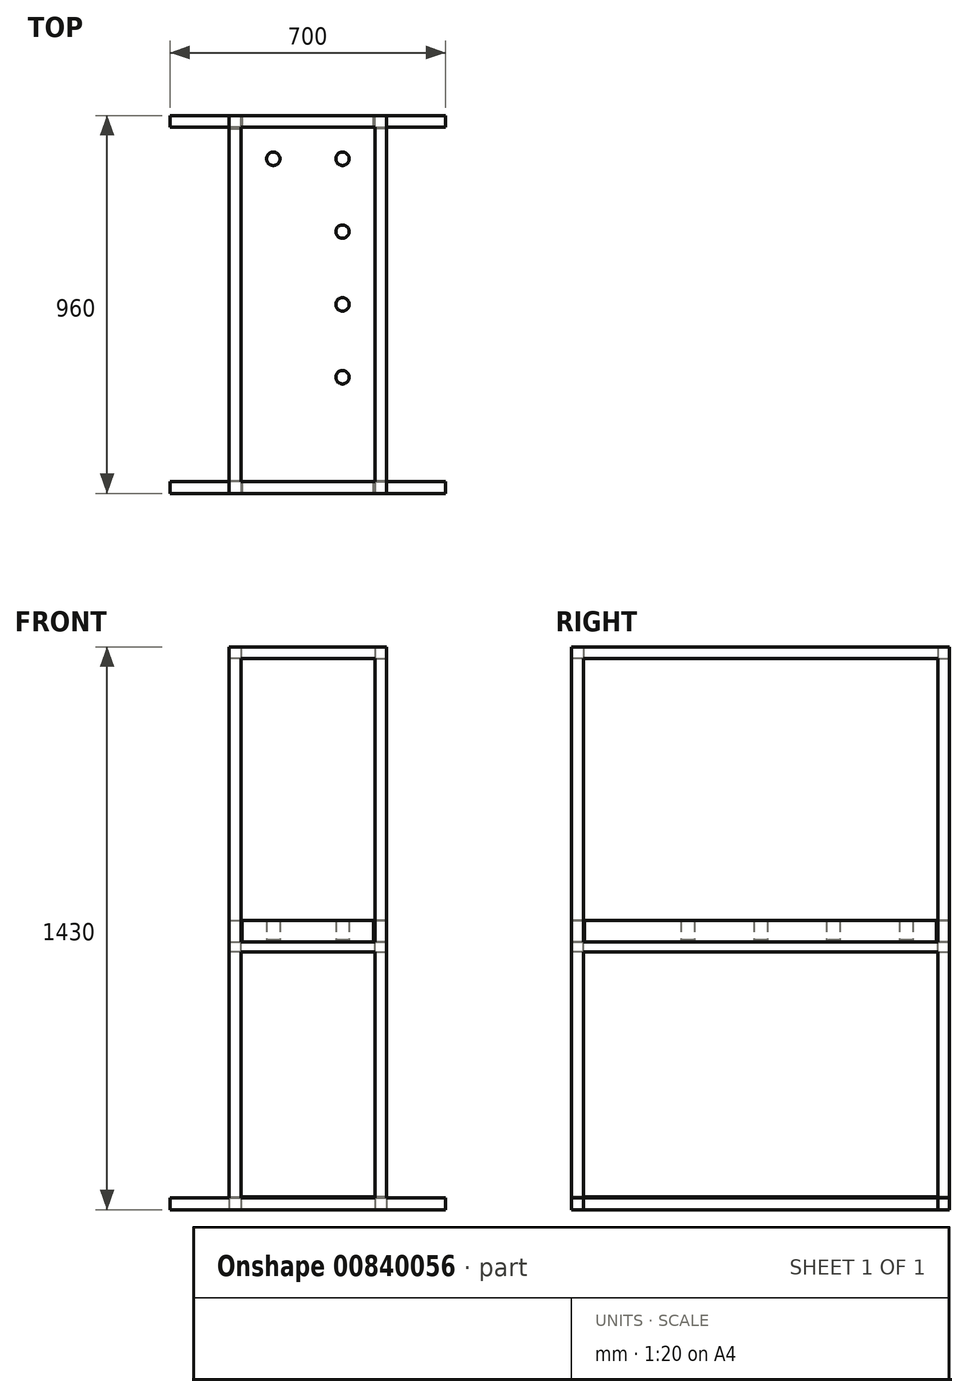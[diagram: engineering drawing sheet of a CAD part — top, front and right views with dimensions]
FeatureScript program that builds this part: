
annotation { "Feature Type Name" : "Feature", "Feature Type Description" : "" }
export const myFeature = defineFeature(function(context is Context, id is Id, definition is map)
    precondition{}
    {
        {
            var Q0;
            Q0=qCreatedBy(makeId("Top.planeOp"),FACE);
            var sketch = newSketch(context, id + "F0", { "sketchPlane" : qUnion([Q0])});
            skLineSegment(sketch, "E0.bottom", {"start": v(200, 480) * mm, "end": v(170, 480) * mm});
            skLineSegment(sketch, "E0.top", {"start": v(200, -480) * mm, "end": v(170, -480) * mm});
            skLineSegment(sketch, "E0.left", {"start": v(200, 480) * mm, "end": v(200, 450) * mm});
            skLineSegment(sketch, "E0.right", {"start": v(-200, 480) * mm, "end": v(-200, 450) * mm});
            skLineSegment(sketch, "E1", {"start": v(170, 450) * mm, "end": v(200, 450) * mm});
            skLineSegment(sketch, "E2", {"start": v(170, 450) * mm, "end": v(170, 480) * mm});
            skLineSegment(sketch, "E3", {"start": v(-170, 450) * mm, "end": v(-170, 480) * mm});
            skLineSegment(sketch, "E4", {"start": v(-170, 450) * mm, "end": v(-200, 450) * mm});
            skLineSegment(sketch, "E5", {"start": v(170, -450) * mm, "end": v(200, -450) * mm});
            skLineSegment(sketch, "E6", {"start": v(170, -450) * mm, "end": v(170, -480) * mm});
            skLineSegment(sketch, "E7", {"start": v(-170, -450) * mm, "end": v(-170, -480) * mm});
            skLineSegment(sketch, "E8", {"start": v(-170, -450) * mm, "end": v(-200, -450) * mm});
            skLineSegment(sketch, "E9.trimOffspring", {"start": v(200, -450) * mm, "end": v(200, -480) * mm});
            skLineSegment(sketch, "E10.trimOffspring", {"start": v(-170, 480) * mm, "end": v(-200, 480) * mm});
            skLineSegment(sketch, "E11.trimOffspring", {"start": v(-200, -450) * mm, "end": v(-200, -480) * mm});
            skLineSegment(sketch, "E12.trimOffspring", {"start": v(-170, -480) * mm, "end": v(-200, -480) * mm});
            skSolve(sketch);
        }
        {
            var Q0;
            Q0 = qSketchRegion(id + "F0", true);
            extrude(context, id + "F1", {"entities" : qUnion([Q0]), "depth" : 1400 * mm, "offsetDistance" : 25 * mm});
        }
        {
            var Q0;
            Q0=qCreatedBy(makeId("Top.planeOp"),FACE);
            var sketch = newSketch(context, id + "F2", { "sketchPlane" : qUnion([Q0])});
            skLineSegment(sketch, "E13", {"start": v(0, 0) * mm, "end": v(0, 511.87) * mm, "construction": true});
            skLineSegment(sketch, "E14.bottom", {"start": v(200, 480) * mm, "end": v(-200, 480) * mm});
            skLineSegment(sketch, "E14.top", {"start": v(200, -480) * mm, "end": v(-200, -480) * mm});
            skLineSegment(sketch, "E14.left", {"start": v(200, 450) * mm, "end": v(200, -450) * mm});
            skLineSegment(sketch, "E14.right", {"start": v(-200, 450) * mm, "end": v(-200, -450) * mm});
            skLineSegment(sketch, "E15.bottom", {"start": v(170, 450) * mm, "end": v(-170, 450) * mm});
            skLineSegment(sketch, "E15.top", {"start": v(170, -450) * mm, "end": v(-170, -450) * mm});
            skLineSegment(sketch, "E15.left", {"start": v(170, 450) * mm, "end": v(170, -450) * mm});
            skLineSegment(sketch, "E15.right", {"start": v(-170, 450) * mm, "end": v(-170, -450) * mm});
            skLineSegment(sketch, "E16", {"start": v(200, -480) * mm, "end": v(350, -480) * mm});
            skLineSegment(sketch, "E17", {"start": v(200, -450) * mm, "end": v(350, -450) * mm});
            skLineSegment(sketch, "E18", {"start": v(350, -450) * mm, "end": v(350, -480) * mm});
            skLineSegment(sketch, "E19.MirrorCS", {"start": v(-200, -450) * mm, "end": v(-350, -450) * mm});
            skLineSegment(sketch, "E20.MirrorCS", {"start": v(-200, -480) * mm, "end": v(-350, -480) * mm});
            skLineSegment(sketch, "E21.MirrorCS", {"start": v(-350, -450) * mm, "end": v(-350, -480) * mm});
            skLineSegment(sketch, "E22", {"start": v(0, 0) * mm, "end": v(-296.78, 0) * mm, "construction": true});
            skPoint(sketch, "E22.endSnap0", {"position": v(-170, 0) * mm});
            skLineSegment(sketch, "E23.MirrorCS", {"start": v(-200, 450) * mm, "end": v(-350, 450) * mm});
            skLineSegment(sketch, "E24.MirrorCS", {"start": v(-200, 480) * mm, "end": v(-350, 480) * mm});
            skLineSegment(sketch, "E25.MirrorCS", {"start": v(-350, 450) * mm, "end": v(-350, 480) * mm});
            skLineSegment(sketch, "E26.MirrorCS", {"start": v(200, 450) * mm, "end": v(350, 450) * mm});
            skLineSegment(sketch, "E27.MirrorCS", {"start": v(200, 480) * mm, "end": v(350, 480) * mm});
            skLineSegment(sketch, "E28.MirrorCS", {"start": v(350, 450) * mm, "end": v(350, 480) * mm});
            skSolve(sketch);
        }
        {
            var Q0;
            Q0=makeQuery(id+"F2.imprint","IMPRINT",FACE,{"disambiguationData":[TD([[makeQuery(id+"F2.imprint","IMPRINT",EDGE,{"derivedFrom":sQuery(id+"F2.wireOp",EDGE,"E14.bottom")}),1.0]])]});
            extrude(context, id + "F3", {"entities" : qUnion([Q0]), "operationType" : NewBodyOperationType.ADD, "depth" : 30 * mm, "offsetDistance" : 25 * mm});
        }
        {
            var Q0;
            Q0=qCreatedBy(makeId("Top.planeOp"),FACE);
            cPlane(context, id + "F4", {"entities" : qUnion([Q0]), "cplaneType" : CPlaneType.OFFSET, "offset" : 680 * mm, "width" : 150 * mm, "height" : 150 * mm});
        }
        {
            var Q0;
            Q0=qCreatedBy(id+"F4.planeOp",FACE);
            var sketch = newSketch(context, id + "F5", { "sketchPlane" : qUnion([Q0])});
            skLineSegment(sketch, "E29", {"start": v(0, 0) * mm, "end": v(0, 511.87) * mm, "construction": true});
            skLineSegment(sketch, "E30.bottom", {"start": v(200, 480) * mm, "end": v(-200, 480) * mm});
            skLineSegment(sketch, "E30.top", {"start": v(200, -480) * mm, "end": v(-200, -480) * mm});
            skLineSegment(sketch, "E30.left", {"start": v(200, 480) * mm, "end": v(200, -480) * mm});
            skLineSegment(sketch, "E30.right", {"start": v(-200, 480) * mm, "end": v(-200, -480) * mm});
            skLineSegment(sketch, "E31.bottom", {"start": v(170, 450) * mm, "end": v(-170, 450) * mm});
            skLineSegment(sketch, "E31.top", {"start": v(170, -450) * mm, "end": v(-170, -450) * mm});
            skLineSegment(sketch, "E31.left", {"start": v(170, 450) * mm, "end": v(170, -450) * mm});
            skLineSegment(sketch, "E31.right", {"start": v(-170, 450) * mm, "end": v(-170, -450) * mm});
            skSolve(sketch);
        }
        {
            var Q0;
            Q0=makeQuery(id+"F5.imprint","IMPRINT",FACE,{"disambiguationData":[TD([[makeQuery(id+"F5.imprint","IMPRINT",EDGE,{"derivedFrom":sQuery(id+"F5.wireOp",EDGE,"E30.bottom")}),1.0]])]});
            extrude(context, id + "F6", {"entities" : qUnion([Q0]), "operationType" : NewBodyOperationType.ADD, "oppositeDirection" : true, "depth" : 25 * mm, "offsetDistance" : 25 * mm});
        }
        {
            var Q0;
            Q0=qCreatedBy(makeId("Top.planeOp"),FACE);
            cPlane(context, id + "F7", {"entities" : qUnion([Q0]), "cplaneType" : CPlaneType.OFFSET, "offset" : 1400 * mm, "width" : 150 * mm, "height" : 150 * mm});
        }
        {
            var Q0;
            Q0=qCreatedBy(id+"F7.planeOp",FACE);
            var sketch = newSketch(context, id + "F8", { "sketchPlane" : qUnion([Q0])});
            skLineSegment(sketch, "E32", {"start": v(0, 0) * mm, "end": v(0, 511.87) * mm, "construction": true});
            skLineSegment(sketch, "E33.bottom", {"start": v(200, 480) * mm, "end": v(-200, 480) * mm});
            skLineSegment(sketch, "E33.top", {"start": v(200, -480) * mm, "end": v(-200, -480) * mm});
            skLineSegment(sketch, "E33.left", {"start": v(200, 480) * mm, "end": v(200, -480) * mm});
            skLineSegment(sketch, "E33.right", {"start": v(-200, 480) * mm, "end": v(-200, -480) * mm});
            skLineSegment(sketch, "E34.bottom", {"start": v(170, 450) * mm, "end": v(-170, 450) * mm});
            skLineSegment(sketch, "E34.top", {"start": v(170, -450) * mm, "end": v(-170, -450) * mm});
            skLineSegment(sketch, "E34.left", {"start": v(170, 450) * mm, "end": v(170, -450) * mm});
            skLineSegment(sketch, "E34.right", {"start": v(-170, 450) * mm, "end": v(-170, -450) * mm});
            skSolve(sketch);
        }
        {
            var Q0;
            Q0=makeQuery(id+"F8.imprint","IMPRINT",FACE,{"disambiguationData":[TD([[makeQuery(id+"F8.imprint","IMPRINT",EDGE,{"derivedFrom":sQuery(id+"F8.wireOp",EDGE,"E33.bottom")}),1.0]])]});
            extrude(context, id + "F9", {"entities" : qUnion([Q0]), "operationType" : NewBodyOperationType.ADD, "depth" : 30 * mm, "offsetDistance" : 25 * mm});
        }
        {
            var Q0;
            Q0=qCreatedBy(id+"F4.planeOp",FACE);
            var sketch = newSketch(context, id + "F10", { "sketchPlane" : qUnion([Q0])});
            skLineSegment(sketch, "E35", {"start": v(-200, 0) * mm, "end": v(-200, -447) * mm});
            skLineSegment(sketch, "E36", {"start": v(-200, -447) * mm, "end": v(-167, -447) * mm});
            skLineSegment(sketch, "E37", {"start": v(-167, -447) * mm, "end": v(-167, -480) * mm});
            skLineSegment(sketch, "E38", {"start": v(-167, -480) * mm, "end": v(167, -480) * mm});
            skLineSegment(sketch, "E39", {"start": v(167, -480) * mm, "end": v(167, -447) * mm});
            skLineSegment(sketch, "E40", {"start": v(167, -447) * mm, "end": v(200, -447) * mm});
            skLineSegment(sketch, "E41", {"start": v(200, -447) * mm, "end": v(200, 447) * mm});
            skLineSegment(sketch, "E42", {"start": v(200, 447) * mm, "end": v(167, 447) * mm});
            skLineSegment(sketch, "E43", {"start": v(167, 447) * mm, "end": v(167, 480) * mm});
            skLineSegment(sketch, "E44", {"start": v(167, 480) * mm, "end": v(-167, 480) * mm});
            skLineSegment(sketch, "E45", {"start": v(-167, 480) * mm, "end": v(-167, 447) * mm});
            skLineSegment(sketch, "E46", {"start": v(-200, 0) * mm, "end": v(-200, 447) * mm});
            skLineSegment(sketch, "E47", {"start": v(-200, 447) * mm, "end": v(-167, 447) * mm});
            skSolve(sketch);
        }
        {
            var Q0;
            Q0=makeQuery(id+"F10.imprint","IMPRINT",FACE,{"disambiguationData":[TD([[makeQuery(id+"F10.imprint","IMPRINT",EDGE,{"derivedFrom":sQuery(id+"F10.wireOp",EDGE,"E35")}),1.0]])]});
            extrude(context, id + "F11", {"entities" : qUnion([Q0]), "depth" : 5 * mm, "offsetDistance" : 25 * mm});
        }
        {
            var Q0;
            Q0=makeQuery(id+"F11.opExtrude","CAP_FACE",FACE,{"disambiguationData":[OSD([sQuery(id+"F10.wireOp",EDGE,"E35"),sQuery(id+"F10.wireOp",EDGE,"E36"),sQuery(id+"F10.wireOp",EDGE,"E37"),sQuery(id+"F10.wireOp",EDGE,"E38"),sQuery(id+"F10.wireOp",EDGE,"E39"),sQuery(id+"F10.wireOp",EDGE,"E40"),sQuery(id+"F10.wireOp",EDGE,"E41"),sQuery(id+"F10.wireOp",EDGE,"E42"),sQuery(id+"F10.wireOp",EDGE,"E43"),sQuery(id+"F10.wireOp",EDGE,"E44"),sQuery(id+"F10.wireOp",EDGE,"E45"),sQuery(id+"F10.wireOp",EDGE,"E46"),sQuery(id+"F10.wireOp",EDGE,"E47")])],"isStart":false});
            var sketch = newSketch(context, id + "F12", { "sketchPlane" : qUnion([Q0])});
            skCircle(sketch, "E48", {"center": v(-88, -370) * mm, "radius": 17 * mm});
            skCircle(sketch, "E49", {"center": v(88, -370) * mm, "radius": 17 * mm});
            skCircle(sketch, "E50.MirrorC", {"center": v(-88, 370) * mm, "radius": 17 * mm});
            skCircle(sketch, "E51.MirrorC", {"center": v(88, 370) * mm, "radius": 17 * mm});
            skCircle(sketch, "E52", {"center": v(-88, -185) * mm, "radius": 17 * mm});
            skCircle(sketch, "E53", {"center": v(-88, 0) * mm, "radius": 17 * mm});
            skCircle(sketch, "E54", {"center": v(-88, 185) * mm, "radius": 17 * mm});
            skCircle(sketch, "E55.MirrorC", {"center": v(88, 185) * mm, "radius": 17 * mm});
            skCircle(sketch, "E56.MirrorC", {"center": v(88, 0) * mm, "radius": 17 * mm});
            skCircle(sketch, "E57.MirrorC", {"center": v(88, -185) * mm, "radius": 17 * mm});
            skSolve(sketch);
        }
        {
            var Q0;
            Q0=makeQuery(id+"F12.imprint","IMPRINT",FACE,{"disambiguationData":[TD([[makeQuery(id+"F12.imprint","IMPRINT",EDGE,{"derivedFrom":sQuery(id+"F12.wireOp",EDGE,"E52")}),1.0]])]});
            var Q1;
            Q1=makeQuery(id+"F12.imprint","IMPRINT",FACE,{"disambiguationData":[TD([[makeQuery(id+"F12.imprint","IMPRINT",EDGE,{"derivedFrom":sQuery(id+"F12.wireOp",EDGE,"E48")}),1.0]])]});
            var Q2;
            Q2=makeQuery(id+"F12.imprint","IMPRINT",FACE,{"disambiguationData":[TD([[makeQuery(id+"F12.imprint","IMPRINT",EDGE,{"derivedFrom":sQuery(id+"F12.wireOp",EDGE,"E57.MirrorC")}),-1.0]])]});
            var Q3;
            Q3=makeQuery(id+"F12.imprint","IMPRINT",FACE,{"disambiguationData":[TD([[makeQuery(id+"F12.imprint","IMPRINT",EDGE,{"derivedFrom":sQuery(id+"F12.wireOp",EDGE,"E49")}),1.0]])]});
            var Q4;
            Q4=makeQuery(id+"F12.imprint","IMPRINT",FACE,{"disambiguationData":[TD([[makeQuery(id+"F12.imprint","IMPRINT",EDGE,{"derivedFrom":sQuery(id+"F12.wireOp",EDGE,"E56.MirrorC")}),-1.0]])]});
            var Q5;
            Q5=makeQuery(id+"F12.imprint","IMPRINT",FACE,{"disambiguationData":[TD([[makeQuery(id+"F12.imprint","IMPRINT",EDGE,{"derivedFrom":sQuery(id+"F12.wireOp",EDGE,"E53")}),1.0]])]});
            var Q6;
            Q6=makeQuery(id+"F12.imprint","IMPRINT",FACE,{"disambiguationData":[TD([[makeQuery(id+"F12.imprint","IMPRINT",EDGE,{"derivedFrom":sQuery(id+"F12.wireOp",EDGE,"E54")}),1.0]])]});
            var Q7;
            Q7=makeQuery(id+"F12.imprint","IMPRINT",FACE,{"disambiguationData":[TD([[makeQuery(id+"F12.imprint","IMPRINT",EDGE,{"derivedFrom":sQuery(id+"F12.wireOp",EDGE,"E55.MirrorC")}),-1.0]])]});
            var Q8;
            Q8=makeQuery(id+"F12.imprint","IMPRINT",FACE,{"disambiguationData":[TD([[makeQuery(id+"F12.imprint","IMPRINT",EDGE,{"derivedFrom":sQuery(id+"F12.wireOp",EDGE,"E51.MirrorC")}),-1.0]])]});
            var Q9;
            Q9=makeQuery(id+"F12.imprint","IMPRINT",FACE,{"disambiguationData":[TD([[makeQuery(id+"F12.imprint","IMPRINT",EDGE,{"derivedFrom":sQuery(id+"F12.wireOp",EDGE,"E50.MirrorC")}),-1.0]])]});
            extrude(context, id + "F13", {"entities" : qUnion([Q0, Q1, Q2, Q3, Q4, Q5, Q6, Q7, Q8, Q9]), "operationType" : NewBodyOperationType.ADD, "depth" : 50 * mm, "offsetDistance" : 25 * mm});
        }
        {
            var Q0;
            Q0=makeQuery(id+"F11.opExtrude","CAP_FACE",FACE,{"disambiguationData":[OSD([sQuery(id+"F10.wireOp",EDGE,"E35"),sQuery(id+"F10.wireOp",EDGE,"E36"),sQuery(id+"F10.wireOp",EDGE,"E37"),sQuery(id+"F10.wireOp",EDGE,"E38"),sQuery(id+"F10.wireOp",EDGE,"E39"),sQuery(id+"F10.wireOp",EDGE,"E40"),sQuery(id+"F10.wireOp",EDGE,"E41"),sQuery(id+"F10.wireOp",EDGE,"E42"),sQuery(id+"F10.wireOp",EDGE,"E43"),sQuery(id+"F10.wireOp",EDGE,"E44"),sQuery(id+"F10.wireOp",EDGE,"E45"),sQuery(id+"F10.wireOp",EDGE,"E46"),sQuery(id+"F10.wireOp",EDGE,"E47")])],"isStart":false});
            var sketch = newSketch(context, id + "F14", { "sketchPlane" : qUnion([Q0])});
            skCircle(sketch, "E58", {"center": v(-88, -370) * mm, "radius": 25 * mm});
            skCircle(sketch, "E59", {"center": v(88, -370) * mm, "radius": 25 * mm});
            skCircle(sketch, "E60.MirrorC", {"center": v(-88, 370) * mm, "radius": 25 * mm});
            skCircle(sketch, "E61.MirrorC", {"center": v(88, 370) * mm, "radius": 25 * mm});
            skCircle(sketch, "E62", {"center": v(-88, -185) * mm, "radius": 25 * mm});
            skCircle(sketch, "E63", {"center": v(-88, 0) * mm, "radius": 25 * mm});
            skCircle(sketch, "E64", {"center": v(-88, 185) * mm, "radius": 25 * mm});
            skCircle(sketch, "E65.MirrorC", {"center": v(88, 185) * mm, "radius": 25 * mm});
            skCircle(sketch, "E66.MirrorC", {"center": v(88, 0) * mm, "radius": 25 * mm});
            skCircle(sketch, "E67.MirrorC", {"center": v(88, -185) * mm, "radius": 25 * mm});
            skSolve(sketch);
        }
        {
            var Q0;
            Q0=makeQuery(id+"F14.imprint","IMPRINT",FACE,{"disambiguationData":[TD([[makeQuery(id+"F14.imprint","IMPRINT",EDGE,{"derivedFrom":sQuery(id+"F14.wireOp",EDGE,"E59")}),1.0]])]});
            var Q1;
            Q1=makeQuery(id+"F14.imprint","IMPRINT",FACE,{"disambiguationData":[TD([[makeQuery(id+"F14.imprint","IMPRINT",EDGE,{"derivedFrom":sQuery(id+"F14.wireOp",EDGE,"E58")}),1.0]])]});
            var Q2;
            Q2=makeQuery(id+"F14.imprint","IMPRINT",FACE,{"disambiguationData":[TD([[makeQuery(id+"F14.imprint","IMPRINT",EDGE,{"derivedFrom":sQuery(id+"F14.wireOp",EDGE,"E62")}),1.0]])]});
            var Q3;
            Q3=makeQuery(id+"F14.imprint","IMPRINT",FACE,{"disambiguationData":[TD([[makeQuery(id+"F14.imprint","IMPRINT",EDGE,{"derivedFrom":sQuery(id+"F14.wireOp",EDGE,"E67.MirrorC")}),-1.0]])]});
            var Q4;
            Q4=makeQuery(id+"F14.imprint","IMPRINT",FACE,{"disambiguationData":[TD([[makeQuery(id+"F14.imprint","IMPRINT",EDGE,{"derivedFrom":sQuery(id+"F14.wireOp",EDGE,"E63")}),1.0]])]});
            var Q5;
            Q5=makeQuery(id+"F14.imprint","IMPRINT",FACE,{"disambiguationData":[TD([[makeQuery(id+"F14.imprint","IMPRINT",EDGE,{"derivedFrom":sQuery(id+"F14.wireOp",EDGE,"E66.MirrorC")}),-1.0]])]});
            var Q6;
            Q6=makeQuery(id+"F14.imprint","IMPRINT",FACE,{"disambiguationData":[TD([[makeQuery(id+"F14.imprint","IMPRINT",EDGE,{"derivedFrom":sQuery(id+"F14.wireOp",EDGE,"E65.MirrorC")}),-1.0]])]});
            var Q7;
            Q7=makeQuery(id+"F14.imprint","IMPRINT",FACE,{"disambiguationData":[TD([[makeQuery(id+"F14.imprint","IMPRINT",EDGE,{"derivedFrom":sQuery(id+"F14.wireOp",EDGE,"E64")}),1.0]])]});
            var Q8;
            Q8=makeQuery(id+"F14.imprint","IMPRINT",FACE,{"disambiguationData":[TD([[makeQuery(id+"F14.imprint","IMPRINT",EDGE,{"derivedFrom":sQuery(id+"F14.wireOp",EDGE,"E60.MirrorC")}),-1.0]])]});
            var Q9;
            Q9=makeQuery(id+"F14.imprint","IMPRINT",FACE,{"disambiguationData":[TD([[makeQuery(id+"F14.imprint","IMPRINT",EDGE,{"derivedFrom":sQuery(id+"F14.wireOp",EDGE,"E61.MirrorC")}),-1.0]])]});
            extrude(context, id + "F15", {"entities" : qUnion([Q0, Q1, Q2, Q3, Q4, Q5, Q6, Q7, Q8, Q9]), "operationType" : NewBodyOperationType.ADD, "depth" : 15 * mm, "offsetDistance" : 25 * mm});
        }
        {
            var Q0;
            {var subQ0=sQuery(id+"F2.wireOp",EDGE,"E14.right");var subQ1=sQuery(id+"F2.wireOp",EDGE,"E15.top");var subQ2=sQuery(id+"F2.wireOp",EDGE,"E15.bottom");var subQ3=sQuery(id+"F2.wireOp",EDGE,"E23.MirrorCS");var subQ4=sQuery(id+"F2.wireOp",EDGE,"E19.MirrorCS");var subQ5=sQuery(id+"F2.wireOp",EDGE,"E15.right");var subQ6=makeQuery(id+"F3.opExtrude","CAP_FACE",FACE,{"disambiguationData":[OSD([sQuery(id+"F2.wireOp",EDGE,"E14.bottom"),sQuery(id+"F2.wireOp",EDGE,"E14.top"),sQuery(id+"F2.wireOp",EDGE,"E14.left"),subQ0,subQ2,subQ1,sQuery(id+"F2.wireOp",EDGE,"E15.left"),subQ5,sQuery(id+"F2.wireOp",EDGE,"E16"),sQuery(id+"F2.wireOp",EDGE,"E17"),sQuery(id+"F2.wireOp",EDGE,"E18"),subQ4,sQuery(id+"F2.wireOp",EDGE,"E20.MirrorCS"),sQuery(id+"F2.wireOp",EDGE,"E21.MirrorCS"),subQ3,sQuery(id+"F2.wireOp",EDGE,"E24.MirrorCS"),sQuery(id+"F2.wireOp",EDGE,"E25.MirrorCS"),sQuery(id+"F2.wireOp",EDGE,"E26.MirrorCS"),sQuery(id+"F2.wireOp",EDGE,"E27.MirrorCS"),sQuery(id+"F2.wireOp",EDGE,"E28.MirrorCS")])],"isStart":false});Q0=makeQuery(id+"F3.boolean.opBoolean","SPLIT",FACE,{"disambiguationData":[TD([makeQuery(id+"F1.opExtrude","SWEPT_FACE",FACE,{"disambiguationData":[OSD([sQuery(id+"F0.wireOp",EDGE,"E0.right")])]}),makeQuery(id+"F1.opExtrude","SWEPT_FACE",FACE,{"disambiguationData":[OSD([sQuery(id+"F0.wireOp",EDGE,"E3")])]}),makeQuery(id+"F1.opExtrude","SWEPT_FACE",FACE,{"disambiguationData":[OSD([sQuery(id+"F0.wireOp",EDGE,"E4")])]}),makeQuery(id+"F1.opExtrude","SWEPT_FACE",FACE,{"disambiguationData":[OSD([sQuery(id+"F0.wireOp",EDGE,"E7")])]}),makeQuery(id+"F1.opExtrude","SWEPT_FACE",FACE,{"disambiguationData":[OSD([sQuery(id+"F0.wireOp",EDGE,"E8")])]}),makeQuery(id+"F1.opExtrude","SWEPT_FACE",FACE,{"disambiguationData":[OSD([sQuery(id+"F0.wireOp",EDGE,"E11.trimOffspring")])]}),subQ6,makeQuery(id+"F3.opExtrude","SWEPT_FACE",FACE,{"disambiguationData":[OSD([subQ0])]}),makeQuery(id+"F3.opExtrude","SWEPT_FACE",FACE,{"disambiguationData":[OSD([subQ2])]}),makeQuery(id+"F3.opExtrude","SWEPT_FACE",FACE,{"disambiguationData":[OSD([subQ1])]}),makeQuery(id+"F3.opExtrude","SWEPT_FACE",FACE,{"disambiguationData":[OSD([subQ5])]}),makeQuery(id+"F3.opExtrude","SWEPT_FACE",FACE,{"disambiguationData":[OSD([subQ4])]}),makeQuery(id+"F3.opExtrude","SWEPT_FACE",FACE,{"disambiguationData":[OSD([subQ3])]})])],"derivedFrom":subQ6});}
            var sketch = newSketch(context, id + "F16", { "sketchPlane" : qUnion([Q0])});
            skLineSegment(sketch, "E68", {"start": v(-200, 43.75) * mm, "end": v(-200, -447) * mm});
            skLineSegment(sketch, "E69", {"start": v(-200, -447) * mm, "end": v(-167, -447) * mm});
            skLineSegment(sketch, "E70", {"start": v(-167, -447) * mm, "end": v(-167, -480) * mm});
            skLineSegment(sketch, "E71", {"start": v(-167, -480) * mm, "end": v(167, -480) * mm});
            skLineSegment(sketch, "E72", {"start": v(167, -480) * mm, "end": v(167, -447) * mm});
            skLineSegment(sketch, "E73", {"start": v(167, -447) * mm, "end": v(200, -447) * mm});
            skLineSegment(sketch, "E74", {"start": v(200, -447) * mm, "end": v(200, 447) * mm});
            skLineSegment(sketch, "E75", {"start": v(200, 447) * mm, "end": v(167, 447) * mm});
            skLineSegment(sketch, "E76", {"start": v(167, 447) * mm, "end": v(167, 480) * mm});
            skLineSegment(sketch, "E77", {"start": v(167, 480) * mm, "end": v(-170, 480) * mm});
            skLineSegment(sketch, "E78", {"start": v(-170, 480) * mm, "end": v(-170, 447) * mm});
            skLineSegment(sketch, "E79", {"start": v(-200, 43.75) * mm, "end": v(-200, 447) * mm});
            skLineSegment(sketch, "E80", {"start": v(-200, 447) * mm, "end": v(-170, 447) * mm});
            skSolve(sketch);
        }
        {
            var Q0;
            Q0 = qSketchRegion(id + "F16", true);
            extrude(context, id + "F17", {"entities" : qUnion([Q0]), "depth" : 3 * mm, "offsetDistance" : 25 * mm});
        }
    });
